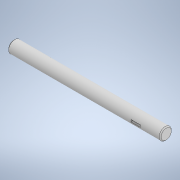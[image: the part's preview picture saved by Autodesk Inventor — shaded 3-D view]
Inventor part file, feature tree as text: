
AUTODESK INVENTOR PART (.ipt)
format: ipt  version: 2021 (Build 250183000, 183)  size: 124,928 bytes
history: native  units: mm
features: other x3, sketch x2, chamfer x1, extrude x1
ambient origin geometry x8: Origin, YZ Plane, XZ Plane, XY Plane, X Axis, Y Axis, Z Axis, Center Point
bodies: Body1 (feature_tree)
feature tree (7):
  other  "Sólido1"
  other  "Revolução1"
  sketch  "Esboço2"  dims[d1=3.0mm d2=90.0deg d3=0.5mm d4=2.0mm d5=45.0deg d6=5.0mm d9=5.0mm d10=12.0mm d11=1.5mm d12=12.0mm d13=1.5mm d14=1.0mm d15=0.0mm d16=0.5mm d17=0.872665mm d18=0.5mm d19=0.872665mm]
  chamfer  "Chanfro1"  Angle=90.0deg  [1 undecoded]
  extrude  "Extrusão1"  Depth=1.0mm TaperAngle=45.0deg
  sketch  "Esboço1"  dims[d0=75.0mm]
  other  "Projetar arestas de corte1"
note: 1 required parameter value undecoded (feature->parameter linkage not recoverable at this tier; creation-order binding heuristic only, values carry confidence <= 0.55)
